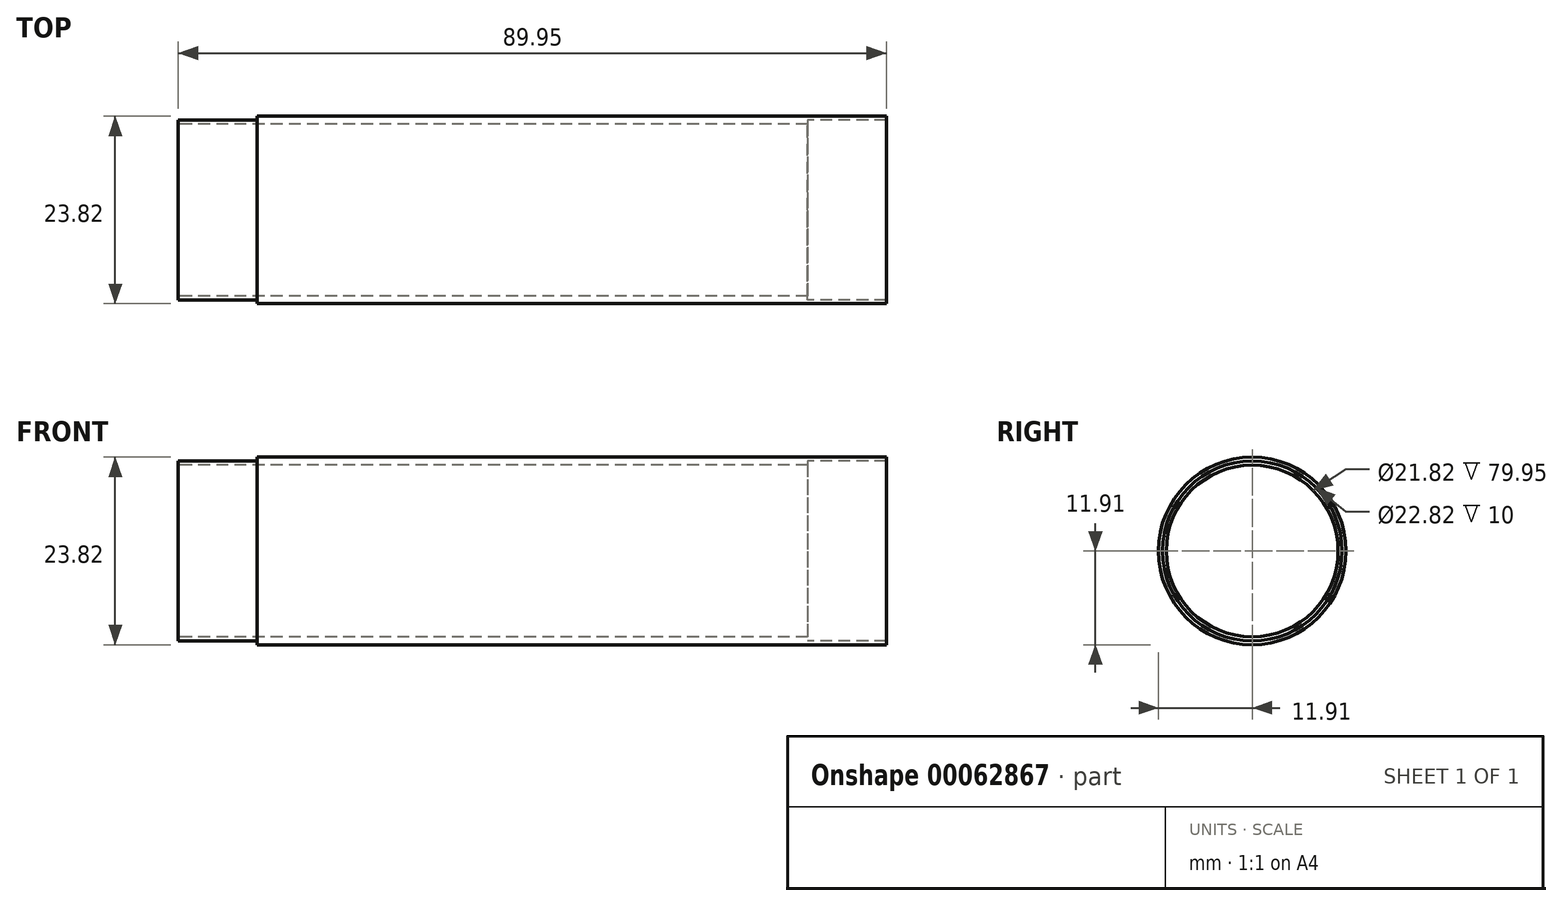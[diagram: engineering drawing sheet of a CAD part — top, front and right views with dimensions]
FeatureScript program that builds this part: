
annotation { "Feature Type Name" : "Feature", "Feature Type Description" : "" }
export const myFeature = defineFeature(function(context is Context, id is Id, definition is map)
    precondition{}
    {
        {
            var Q0;
            Q0=qCreatedBy(makeId("Front.planeOp"),FACE);
            var sketch = newSketch(context, id + "F0", { "sketchPlane" : qUnion([Q0])});
            skLineSegment(sketch, "E0", {"start": v(-32.25, 11.91) * mm, "end": v(47.7, 11.91) * mm});
            skLineSegment(sketch, "E1", {"start": v(47.7, 11.91) * mm, "end": v(37.7, 11.91) * mm});
            skLineSegment(sketch, "E2", {"start": v(-32.25, 11.91) * mm, "end": v(-32.25, 11.41) * mm});
            skLineSegment(sketch, "E3", {"start": v(-32.25, 11.41) * mm, "end": v(-42.25, 11.41) * mm});
            skLineSegment(sketch, "E4", {"start": v(37.7, 11.91) * mm, "end": v(37.7, 11.41) * mm});
            skLineSegment(sketch, "E5", {"start": v(47.7, 11.91) * mm, "end": v(47.7, 11.41) * mm});
            skLineSegment(sketch, "E6", {"start": v(47.7, 11.41) * mm, "end": v(37.7, 11.41) * mm});
            skLineSegment(sketch, "E7", {"start": v(-32.25, 11.91) * mm, "end": v(-32.25, 10.91) * mm});
            skLineSegment(sketch, "E8", {"start": v(37.7, 11.91) * mm, "end": v(37.7, 10.91) * mm});
            skPoint(sketch, "E8.endSnap0", {"position": v(37.7, 11.66) * mm});
            skLineSegment(sketch, "E9", {"start": v(-32.25, 10.91) * mm, "end": v(37.7, 10.91) * mm});
            skLineSegment(sketch, "E10", {"start": v(-42.25, 11.41) * mm, "end": v(-42.25, 10.91) * mm});
            skLineSegment(sketch, "E11", {"start": v(-42.25, 10.91) * mm, "end": v(-32.25, 10.91) * mm});
            skLineSegment(sketch, "E12", {"start": v(0, 11.91) * mm, "end": v(0, 0) * mm});
            skLineSegment(sketch, "E13", {"start": v(0, 0) * mm, "end": v(37.9, 0) * mm});
            skSolve(sketch);
        }
        {
            var Q0;
            Q0 = qSketchRegion(id + "F0", true);
            var Q1;
            Q1=sQuery(id+"F0.wireOp",EDGE,"E13");
            revolve(context, id + "F1", {"entities" : qUnion([Q0]), "axis" : qUnion([Q1]), "revolveType" : RevolveType.FULL});
        }
    });
